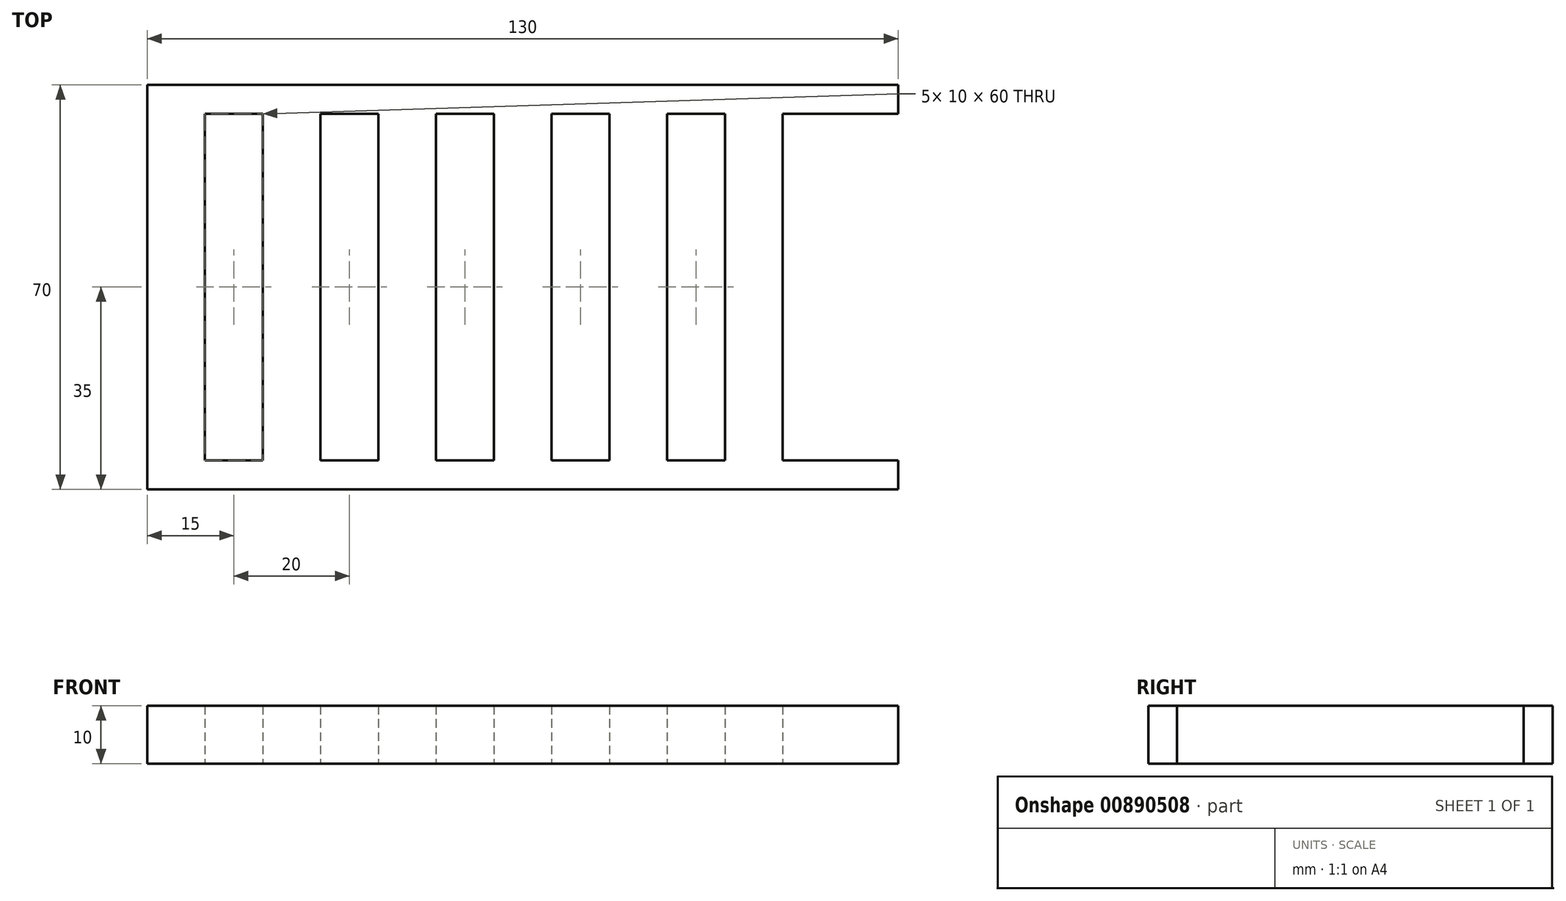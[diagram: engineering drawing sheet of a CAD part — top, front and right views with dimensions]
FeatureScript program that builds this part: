
annotation { "Feature Type Name" : "Feature", "Feature Type Description" : "" }
export const myFeature = defineFeature(function(context is Context, id is Id, definition is map)
    precondition{}
    {
        {
            var Q0;
            Q0=qCreatedBy(makeId("Top.planeOp"),FACE);
            var sketch = newSketch(context, id + "F0", { "sketchPlane" : qUnion([Q0])});
            skLineSegment(sketch, "E0.bottom", {"start": v(65, 35) * mm, "end": v(-65, 35) * mm});
            skLineSegment(sketch, "E0.top", {"start": v(65, -35) * mm, "end": v(-65, -35) * mm});
            skLineSegment(sketch, "E0.left", {"start": v(65, 35) * mm, "end": v(65, -35) * mm});
            skLineSegment(sketch, "E0.right", {"start": v(-65, 35) * mm, "end": v(-65, -35) * mm});
            skPoint(sketch, "E0.middle", {"position": v(0, 0) * mm});
            skLineSegment(sketch, "E1", {"start": v(-65, -35) * mm, "end": v(-65, -30) * mm});
            skLineSegment(sketch, "E2", {"start": v(-65, -30) * mm, "end": v(65, -30) * mm});
            skLineSegment(sketch, "E3", {"start": v(-65, 35) * mm, "end": v(-65, 30) * mm});
            skLineSegment(sketch, "E4", {"start": v(-65, 30) * mm, "end": v(65, 30) * mm});
            skLineSegment(sketch, "E5", {"start": v(65, 30) * mm, "end": v(55, 30) * mm});
            skLineSegment(sketch, "E6", {"start": v(55, 30) * mm, "end": v(55, -30) * mm});
            skLineSegment(sketch, "E7", {"start": v(55, -30) * mm, "end": v(45, -30) * mm});
            skLineSegment(sketch, "E8", {"start": v(45, -30) * mm, "end": v(45, 30) * mm});
            skLineSegment(sketch, "E9", {"start": v(45, 30) * mm, "end": v(35, 30) * mm});
            skLineSegment(sketch, "E10", {"start": v(35, 30) * mm, "end": v(35, -30) * mm});
            skLineSegment(sketch, "E11", {"start": v(35, -30) * mm, "end": v(25, -30) * mm});
            skLineSegment(sketch, "E12", {"start": v(25, -30) * mm, "end": v(25, 30) * mm});
            skLineSegment(sketch, "E13", {"start": v(25, 30) * mm, "end": v(15, 30) * mm});
            skLineSegment(sketch, "E14", {"start": v(15, 30) * mm, "end": v(15, -30) * mm});
            skLineSegment(sketch, "E15", {"start": v(15, -30) * mm, "end": v(5, -30) * mm});
            skLineSegment(sketch, "E16", {"start": v(5, -30) * mm, "end": v(5, 30) * mm});
            skLineSegment(sketch, "E17", {"start": v(5, 30) * mm, "end": v(-5, 30) * mm});
            skLineSegment(sketch, "E18", {"start": v(-5, 30) * mm, "end": v(-5, -30) * mm});
            skLineSegment(sketch, "E19", {"start": v(-5, -30) * mm, "end": v(-15, -30) * mm});
            skLineSegment(sketch, "E20", {"start": v(-15, -30) * mm, "end": v(-15, 30) * mm});
            skLineSegment(sketch, "E21", {"start": v(-15, 30) * mm, "end": v(-25, 30) * mm});
            skLineSegment(sketch, "E22", {"start": v(-25, 30) * mm, "end": v(-25, -30) * mm});
            skLineSegment(sketch, "E23", {"start": v(-25, -30) * mm, "end": v(-35, -30) * mm});
            skLineSegment(sketch, "E24", {"start": v(-35, -30) * mm, "end": v(-35, 30) * mm});
            skLineSegment(sketch, "E25", {"start": v(-35, 30) * mm, "end": v(-45, 30) * mm});
            skLineSegment(sketch, "E26", {"start": v(-45, 30) * mm, "end": v(-45, -30) * mm});
            skLineSegment(sketch, "E27", {"start": v(-45, -30) * mm, "end": v(-55, -30) * mm});
            skLineSegment(sketch, "E28", {"start": v(-55, -30) * mm, "end": v(-55, 30) * mm});
            skSolve(sketch);
        }
        {
            var Q0;
            {var subQ0=sQuery(id+"F0.wireOp",EDGE,"E0.right");Q0=makeQuery(id+"F0.imprint","IMPRINT",FACE,{"disambiguationData":[TD([[makeQuery(id+"F0.imprint","IMPRINT",EDGE,{"derivedFrom":subQ0}),1.0]])]});}
            var Q1;
            {var subQ0=sQuery(id+"F0.wireOp",EDGE,"E24");Q1=makeQuery(id+"F0.imprint","IMPRINT",FACE,{"disambiguationData":[TD([[makeQuery(id+"F0.imprint","IMPRINT",EDGE,{"derivedFrom":subQ0}),1.0]])]});}
            var Q2;
            {var subQ8=sQuery(id+"F0.wireOp",EDGE,"E0.bottom");Q2=makeQuery(id+"F0.imprint","IMPRINT",FACE,{"disambiguationData":[TD([[makeQuery(id+"F0.imprint","IMPRINT",EDGE,{"derivedFrom":subQ8}),1.0]])]});}
            var Q3;
            {var subQ0=sQuery(id+"F0.wireOp",EDGE,"E20");Q3=makeQuery(id+"F0.imprint","IMPRINT",FACE,{"disambiguationData":[TD([[makeQuery(id+"F0.imprint","IMPRINT",EDGE,{"derivedFrom":subQ0}),1.0]])]});}
            var Q4;
            {var subQ0=sQuery(id+"F0.wireOp",EDGE,"E16");Q4=makeQuery(id+"F0.imprint","IMPRINT",FACE,{"disambiguationData":[TD([[makeQuery(id+"F0.imprint","IMPRINT",EDGE,{"derivedFrom":subQ0}),1.0]])]});}
            var Q5;
            {var subQ0=sQuery(id+"F0.wireOp",EDGE,"E12");Q5=makeQuery(id+"F0.imprint","IMPRINT",FACE,{"disambiguationData":[TD([[makeQuery(id+"F0.imprint","IMPRINT",EDGE,{"derivedFrom":subQ0}),1.0]])]});}
            var Q6;
            {var subQ0=sQuery(id+"F0.wireOp",EDGE,"E8");Q6=makeQuery(id+"F0.imprint","IMPRINT",FACE,{"disambiguationData":[TD([[makeQuery(id+"F0.imprint","IMPRINT",EDGE,{"derivedFrom":subQ0}),1.0]])]});}
            var Q7;
            {var subQ3=sQuery(id+"F0.wireOp",EDGE,"E5");Q7=makeQuery(id+"F0.imprint","IMPRINT",FACE,{"disambiguationData":[TD([[makeQuery(id+"F0.imprint","IMPRINT",EDGE,{"derivedFrom":subQ3}),1.0]])]});}
            var Q8;
            {var subQ9=sQuery(id+"F0.wireOp",EDGE,"E0.top");Q8=makeQuery(id+"F0.imprint","IMPRINT",FACE,{"disambiguationData":[TD([[makeQuery(id+"F0.imprint","IMPRINT",EDGE,{"derivedFrom":subQ9}),-1.0]])]});}
            extrude(context, id + "F1", {"entities" : qUnion([Q0, Q1, Q2, Q3, Q4, Q5, Q6, Q7, Q8]), "depth" : 10 * mm, "offsetDistance" : 25 * mm});
        }
    });
